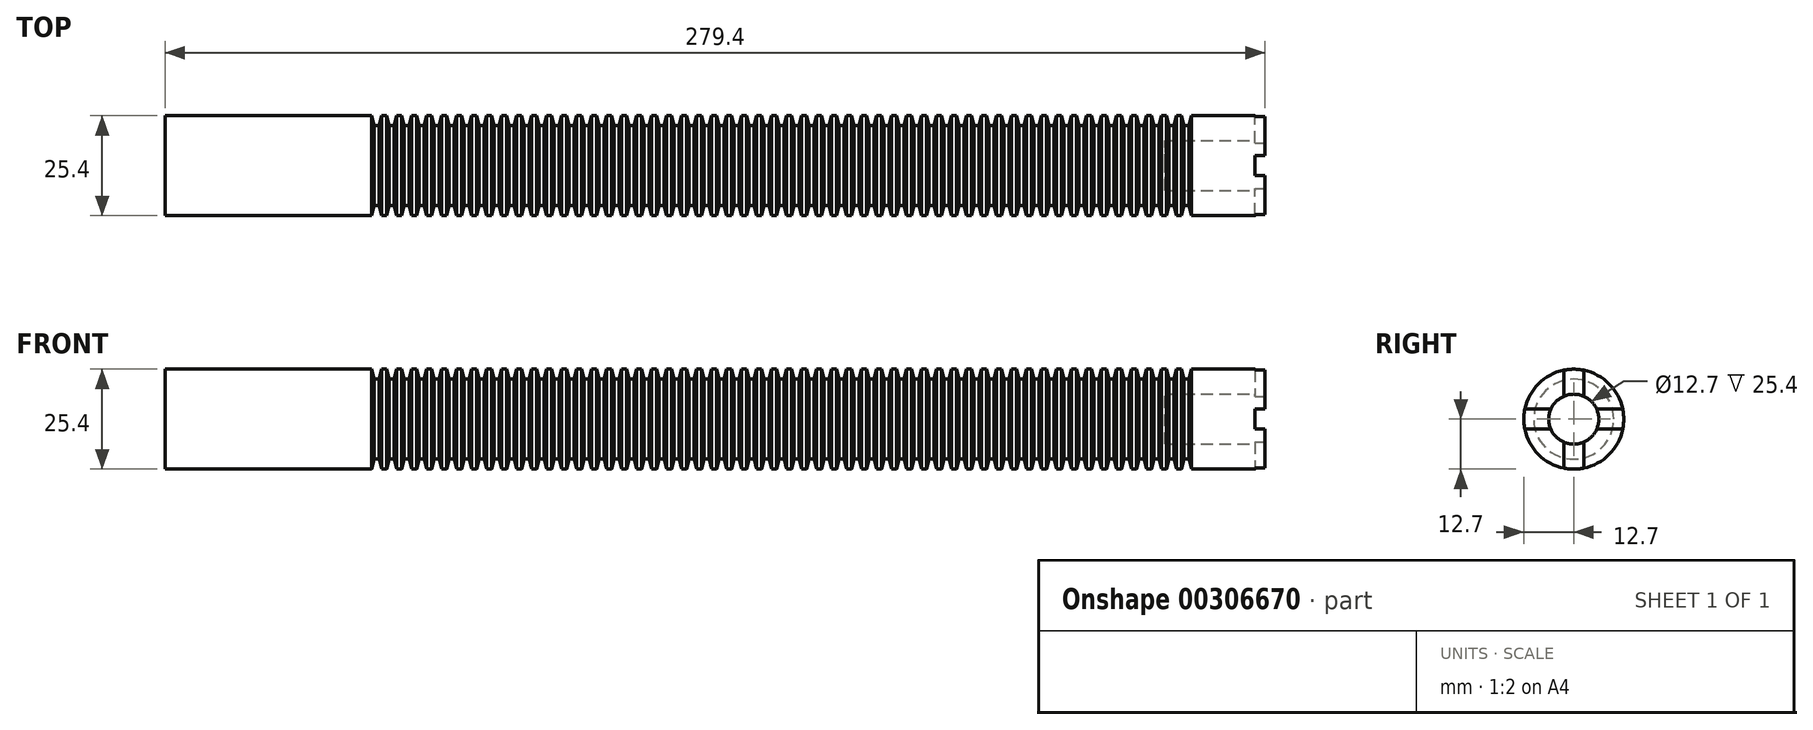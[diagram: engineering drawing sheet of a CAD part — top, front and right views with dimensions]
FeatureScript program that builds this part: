
annotation { "Feature Type Name" : "Feature", "Feature Type Description" : "" }
export const myFeature = defineFeature(function(context is Context, id is Id, definition is map)
    precondition{}
    {
        {
            var Q0;
            Q0=qCreatedBy(makeId("Front.planeOp"),FACE);
            var sketch = newSketch(context, id + "F0", { "sketchPlane" : qUnion([Q0])});
            skLineSegment(sketch, "E0", {"start": v(0, 0) * mm, "end": v(0, 12.7) * mm});
            skLineSegment(sketch, "E1", {"start": v(0, 12.7) * mm, "end": v(279.4, 12.7) * mm});
            skLineSegment(sketch, "E2", {"start": v(279.4, 12.7) * mm, "end": v(279.4, 0) * mm});
            skLineSegment(sketch, "E3", {"start": v(279.4, 0) * mm, "end": v(0, 0) * mm});
            skSolve(sketch);
        }
        {
            var Q0;
            Q0=makeQuery(id+"F0.imprint","IMPRINT",FACE,{"disambiguationData":[TD([[makeQuery(id+"F0.imprint","IMPRINT",EDGE,{"derivedFrom":sQuery(id+"F0.wireOp",EDGE,"E0")}),-1.0]])]});
            var Q1;
            Q1=sQuery(id+"F0.wireOp",EDGE,"E3");
            revolve(context, id + "F1", {"entities" : qUnion([Q0]), "axis" : qUnion([Q1]), "revolveType" : RevolveType.FULL});
        }
        {
            var Q0;
            Q0=makeQuery(id+"F1.opRevolve","SWEPT_FACE",FACE,{"disambiguationData":[OSD([sQuery(id+"F0.wireOp",EDGE,"E2")])]});
            var sketch = newSketch(context, id + "F2", { "sketchPlane" : qUnion([Q0])});
            skLineSegment(sketch, "E4.0", {"start": v(-12.7, -2.54) * mm, "end": v(-2.54, -2.54) * mm});
            skLineSegment(sketch, "E5.0", {"start": v(-12.7, 2.54) * mm, "end": v(-2.54, 2.54) * mm});
            skLineSegment(sketch, "E6.0", {"start": v(-2.54, 12.7) * mm, "end": v(-2.54, 2.54) * mm});
            skLineSegment(sketch, "E7.0", {"start": v(2.54, 12.7) * mm, "end": v(2.54, 2.54) * mm});
            skLineSegment(sketch, "E8.trimOffspring", {"start": v(2.54, 2.54) * mm, "end": v(12.7, 2.54) * mm});
            skLineSegment(sketch, "E9.trimOffspring", {"start": v(-2.54, -2.54) * mm, "end": v(-2.54, -12.7) * mm});
            skLineSegment(sketch, "E10.trimOffspring", {"start": v(2.54, -2.54) * mm, "end": v(12.7, -2.54) * mm});
            skLineSegment(sketch, "E11.trimOffspring", {"start": v(2.54, -2.54) * mm, "end": v(2.54, -12.7) * mm});
            skLineSegment(sketch, "E12", {"start": v(12.7, 2.54) * mm, "end": v(12.7, -2.54) * mm});
            skLineSegment(sketch, "E13", {"start": v(2.54, -12.7) * mm, "end": v(-2.54, -12.7) * mm});
            skLineSegment(sketch, "E14", {"start": v(-12.7, -2.54) * mm, "end": v(-12.7, 2.54) * mm});
            skLineSegment(sketch, "E15", {"start": v(-2.54, 12.7) * mm, "end": v(2.54, 12.7) * mm});
            skSolve(sketch);
        }
        {
            var Q0;
            {var subQ0=sQuery(id+"F2.wireOp",EDGE,"E14");var subQ1=sQuery(id+"F2.wireOp",EDGE,"E4.0");var subQ2=makeQuery(id+"F2.imprint","INTERSECT",VERTEX,{"derivedFrom":[subQ1,subQ0]});Q0=makeQuery(id+"F2.imprint","IMPRINT",FACE,{"disambiguationData":[TD([[makeQuery(id+"F2.imprint","IMPRINT",EDGE,{"disambiguationData":[TD([[subQ2,-1.0]])],"derivedFrom":subQ1}),1.0]])]});}
            var Q1;
            {var subQ0=sQuery(id+"F2.wireOp",EDGE,"E14");var subQ1=sQuery(id+"F2.wireOp",EDGE,"E5.0");var subQ2=makeQuery(id+"F2.imprint","INTERSECT",VERTEX,{"derivedFrom":[subQ1,subQ0]});Q1=makeQuery(id+"F2.imprint","IMPRINT",FACE,{"disambiguationData":[TD([[makeQuery(id+"F2.imprint","IMPRINT",EDGE,{"disambiguationData":[TD([[subQ2,-1.0]])],"derivedFrom":subQ1}),-1.0]])]});}
            var Q2;
            {var subQ0=sQuery(id+"F2.wireOp",EDGE,"E15");var subQ1=sQuery(id+"F2.wireOp",EDGE,"E6.0");var subQ2=makeQuery(id+"F2.imprint","INTERSECT",VERTEX,{"derivedFrom":[subQ1,subQ0]});Q2=makeQuery(id+"F2.imprint","IMPRINT",FACE,{"disambiguationData":[TD([[makeQuery(id+"F2.imprint","IMPRINT",EDGE,{"disambiguationData":[TD([[subQ2,-1.0]])],"derivedFrom":subQ1}),1.0]])]});}
            var Q3;
            {var subQ0=sQuery(id+"F2.wireOp",EDGE,"E15");var subQ1=sQuery(id+"F2.wireOp",EDGE,"E7.0");var subQ2=makeQuery(id+"F2.imprint","INTERSECT",VERTEX,{"derivedFrom":[subQ1,subQ0]});Q3=makeQuery(id+"F2.imprint","IMPRINT",FACE,{"disambiguationData":[TD([[makeQuery(id+"F2.imprint","IMPRINT",EDGE,{"disambiguationData":[TD([[subQ2,-1.0]])],"derivedFrom":subQ1}),-1.0]])]});}
            var Q4;
            {var subQ0=sQuery(id+"F2.wireOp",EDGE,"E12");var subQ1=sQuery(id+"F2.wireOp",EDGE,"E8.trimOffspring");var subQ2=makeQuery(id+"F2.imprint","INTERSECT",VERTEX,{"derivedFrom":[subQ1,subQ0]});Q4=makeQuery(id+"F2.imprint","IMPRINT",FACE,{"disambiguationData":[TD([[makeQuery(id+"F2.imprint","IMPRINT",EDGE,{"disambiguationData":[TD([[subQ2,1.0]])],"derivedFrom":subQ1}),-1.0]])]});}
            var Q5;
            {var subQ0=sQuery(id+"F2.wireOp",EDGE,"E13");var subQ1=sQuery(id+"F2.wireOp",EDGE,"E9.trimOffspring");var subQ2=makeQuery(id+"F2.imprint","INTERSECT",VERTEX,{"derivedFrom":[subQ1,subQ0]});Q5=makeQuery(id+"F2.imprint","IMPRINT",FACE,{"disambiguationData":[TD([[makeQuery(id+"F2.imprint","IMPRINT",EDGE,{"disambiguationData":[TD([[subQ2,1.0]])],"derivedFrom":subQ1}),1.0]])]});}
            var Q6;
            {var subQ0=sQuery(id+"F2.wireOp",EDGE,"E12");var subQ1=sQuery(id+"F2.wireOp",EDGE,"E10.trimOffspring");var subQ2=makeQuery(id+"F2.imprint","INTERSECT",VERTEX,{"derivedFrom":[subQ1,subQ0]});Q6=makeQuery(id+"F2.imprint","IMPRINT",FACE,{"disambiguationData":[TD([[makeQuery(id+"F2.imprint","IMPRINT",EDGE,{"disambiguationData":[TD([[subQ2,1.0]])],"derivedFrom":subQ1}),1.0]])]});}
            var Q7;
            {var subQ0=sQuery(id+"F2.wireOp",EDGE,"E13");var subQ1=sQuery(id+"F2.wireOp",EDGE,"E11.trimOffspring");var subQ2=makeQuery(id+"F2.imprint","INTERSECT",VERTEX,{"derivedFrom":[subQ1,subQ0]});Q7=makeQuery(id+"F2.imprint","IMPRINT",FACE,{"disambiguationData":[TD([[makeQuery(id+"F2.imprint","IMPRINT",EDGE,{"disambiguationData":[TD([[subQ2,1.0]])],"derivedFrom":subQ1}),-1.0]])]});}
            var Q8;
            {var subQ0=sQuery(id+"F2.wireOp",EDGE,"E4.0");var subQ8=sQuery(id+"F2.wireOp",EDGE,"E9.trimOffspring");var subQ9=makeQuery(id+"F2.imprint","INTERSECT",VERTEX,{"derivedFrom":[subQ0,subQ8]});Q8=makeQuery(id+"F2.imprint","IMPRINT",FACE,{"disambiguationData":[TD([[makeQuery(id+"F2.imprint","IMPRINT",EDGE,{"disambiguationData":[TD([[subQ9,1.0]])],"derivedFrom":subQ0}),1.0]])]});}
            extrude(context, id + "F3", {"entities" : qUnion([Q0, Q1, Q2, Q3, Q4, Q5, Q6, Q7, Q8]), "operationType" : NewBodyOperationType.REMOVE, "oppositeDirection" : true, "depth" : 2.54 * mm});
        }
        {
            var Q0;
            Q0=makeQuery(id+"F3.boolean.opBoolean","SPLIT",FACE,{"disambiguationData":[TD([makeQuery(id+"F3.opExtrude","SWEPT_FACE",FACE,{"disambiguationData":[OSD([sQuery(id+"F2.wireOp",EDGE,"E5.0")])]})])],"derivedFrom":makeQuery(id+"F1.opRevolve","SWEPT_FACE",FACE,{"disambiguationData":[OSD([sQuery(id+"F0.wireOp",EDGE,"E2")])]})});
            var sketch = newSketch(context, id + "F4", { "sketchPlane" : qUnion([Q0])});
            skArc(sketch, "E16.0", {"start": v(-2.54, 12.44) * mm, "mid": v(-8.98, 8.98) * mm, "end": v(-12.44, 2.54) * mm});
            skCircle(sketch, "E17", {"center": v(0, 0) * mm, "radius": 6.35 * mm});
            skSolve(sketch);
        }
        {
            var Q0;
            {var subQ0=sQuery(id+"F4.wireOp",EDGE,"E17");var subQ1=makeQuery(id+"F3.boolean.opBoolean","COPY",EDGE,{"derivedFrom":makeQuery(id+"F3.opExtrude","CAP_EDGE",EDGE,{"disambiguationData":[OSD([sQuery(id+"F2.wireOp",EDGE,"E5.0")])],"isStart":true})});var subQ2=makeQuery(id+"F4.imprint","INTERSECT",VERTEX,{"derivedFrom":[subQ1,subQ0]});Q0=makeQuery(id+"F4.imprint","IMPRINT",FACE,{"disambiguationData":[TD([[makeQuery(id+"F4.imprint","IMPRINT",EDGE,{"disambiguationData":[TD([[subQ2,1.0]])],"derivedFrom":subQ0}),1.0]])]});}
            var Q1;
            {var subQ0=sQuery(id+"F4.wireOp",EDGE,"E17");var subQ1=makeQuery(id+"F3.boolean.opBoolean","COPY",EDGE,{"derivedFrom":makeQuery(id+"F3.opExtrude","CAP_EDGE",EDGE,{"disambiguationData":[OSD([sQuery(id+"F2.wireOp",EDGE,"E5.0")])],"isStart":true})});var subQ2=makeQuery(id+"F4.imprint","INTERSECT",VERTEX,{"derivedFrom":[subQ1,subQ0]});Q1=makeQuery(id+"F4.imprint","IMPRINT",FACE,{"disambiguationData":[TD([[makeQuery(id+"F4.imprint","IMPRINT",EDGE,{"disambiguationData":[TD([[subQ2,-1.0]])],"derivedFrom":subQ0}),1.0]])]});}
            extrude(context, id + "F5", {"entities" : qUnion([Q0, Q1]), "operationType" : NewBodyOperationType.REMOVE, "oppositeDirection" : true, "depth" : 25.4 * mm});
        }
        {
            var Q0;
            Q0=qCreatedBy(makeId("Front.planeOp"),FACE);
            var sketch = newSketch(context, id + "F6", { "sketchPlane" : qUnion([Q0])});
            skLineSegment(sketch, "E18", {"start": v(276.86, -12.7) * mm, "end": v(0, -12.7) * mm});
            skLineSegment(sketch, "E19", {"start": v(279.4, 12.7) * mm, "end": v(260.35, 12.7) * mm, "construction": true});
            skLineSegment(sketch, "E20", {"start": v(260.35, 12.7) * mm, "end": v(260.35, -12.7) * mm, "construction": true});
            skLineSegment(sketch, "E21", {"start": v(0.03, 12.7) * mm, "end": v(52.48, 12.7) * mm, "construction": true});
            skLineSegment(sketch, "E22", {"start": v(52.48, 12.7) * mm, "end": v(52.48, 10.16) * mm, "construction": true});
            skLineSegment(sketch, "E23", {"start": v(52.48, 12.7) * mm, "end": v(53.12, 10.16) * mm});
            skLineSegment(sketch, "E24", {"start": v(53.12, 10.16) * mm, "end": v(54.39, 10.16) * mm});
            skLineSegment(sketch, "E25", {"start": v(54.39, 10.16) * mm, "end": v(55.02, 12.7) * mm});
            skLineSegment(sketch, "E26", {"start": v(55.02, 12.7) * mm, "end": v(52.48, 12.7) * mm});
            skLineSegment(sketch, "E27", {"start": v(52.48, 12.7) * mm, "end": v(55.02, 12.7) * mm});
            skLineSegment(sketch, "E28.1.0.0", {"start": v(58.2, 10.16) * mm, "end": v(58.83, 12.7) * mm});
            skLineSegment(sketch, "E28.1.0.1", {"start": v(56.93, 10.16) * mm, "end": v(58.2, 10.16) * mm});
            skLineSegment(sketch, "E28.1.0.2", {"start": v(56.3, 12.7) * mm, "end": v(56.93, 10.16) * mm});
            skLineSegment(sketch, "E28.1.0.3", {"start": v(56.3, 12.7) * mm, "end": v(58.83, 12.7) * mm});
            skLineSegment(sketch, "E28.2.0.0", {"start": v(62, 10.16) * mm, "end": v(62.64, 12.7) * mm});
            skLineSegment(sketch, "E28.2.0.1", {"start": v(60.74, 10.16) * mm, "end": v(62, 10.16) * mm});
            skLineSegment(sketch, "E28.2.0.2", {"start": v(60.1, 12.7) * mm, "end": v(60.74, 10.16) * mm});
            skLineSegment(sketch, "E28.2.0.3", {"start": v(60.1, 12.7) * mm, "end": v(62.64, 12.7) * mm});
            skLineSegment(sketch, "E28.3.0.0", {"start": v(65.82, 10.16) * mm, "end": v(66.45, 12.7) * mm});
            skLineSegment(sketch, "E28.3.0.1", {"start": v(64.55, 10.16) * mm, "end": v(65.82, 10.16) * mm});
            skLineSegment(sketch, "E28.3.0.2", {"start": v(63.91, 12.7) * mm, "end": v(64.55, 10.16) * mm});
            skLineSegment(sketch, "E28.3.0.3", {"start": v(63.91, 12.7) * mm, "end": v(66.45, 12.7) * mm});
            skLineSegment(sketch, "E28.4.0.0", {"start": v(69.63, 10.16) * mm, "end": v(70.26, 12.7) * mm});
            skLineSegment(sketch, "E28.4.0.1", {"start": v(68.36, 10.16) * mm, "end": v(69.63, 10.16) * mm});
            skLineSegment(sketch, "E28.4.0.2", {"start": v(67.72, 12.7) * mm, "end": v(68.36, 10.16) * mm});
            skLineSegment(sketch, "E28.4.0.3", {"start": v(67.72, 12.7) * mm, "end": v(70.26, 12.7) * mm});
            skLineSegment(sketch, "E28.5.0.0", {"start": v(73.44, 10.16) * mm, "end": v(74.07, 12.7) * mm});
            skLineSegment(sketch, "E28.5.0.1", {"start": v(72.17, 10.16) * mm, "end": v(73.44, 10.16) * mm});
            skLineSegment(sketch, "E28.5.0.2", {"start": v(71.53, 12.7) * mm, "end": v(72.17, 10.16) * mm});
            skLineSegment(sketch, "E28.5.0.3", {"start": v(71.53, 12.7) * mm, "end": v(74.07, 12.7) * mm});
            skLineSegment(sketch, "E28.6.0.0", {"start": v(77.25, 10.16) * mm, "end": v(77.88, 12.7) * mm});
            skLineSegment(sketch, "E28.6.0.1", {"start": v(75.98, 10.16) * mm, "end": v(77.25, 10.16) * mm});
            skLineSegment(sketch, "E28.6.0.2", {"start": v(75.34, 12.7) * mm, "end": v(75.98, 10.16) * mm});
            skLineSegment(sketch, "E28.6.0.3", {"start": v(75.34, 12.7) * mm, "end": v(77.88, 12.7) * mm});
            skLineSegment(sketch, "E28.7.0.0", {"start": v(81.06, 10.16) * mm, "end": v(81.7, 12.7) * mm});
            skLineSegment(sketch, "E28.7.0.1", {"start": v(79.8, 10.16) * mm, "end": v(81.06, 10.16) * mm});
            skLineSegment(sketch, "E28.7.0.2", {"start": v(79.15, 12.7) * mm, "end": v(79.8, 10.16) * mm});
            skLineSegment(sketch, "E28.7.0.3", {"start": v(79.15, 12.7) * mm, "end": v(81.7, 12.7) * mm});
            skLineSegment(sketch, "E28.8.0.0", {"start": v(84.87, 10.16) * mm, "end": v(85.5, 12.7) * mm});
            skLineSegment(sketch, "E28.8.0.1", {"start": v(83.6, 10.16) * mm, "end": v(84.87, 10.16) * mm});
            skLineSegment(sketch, "E28.8.0.2", {"start": v(82.96, 12.7) * mm, "end": v(83.6, 10.16) * mm});
            skLineSegment(sketch, "E28.8.0.3", {"start": v(82.96, 12.7) * mm, "end": v(85.5, 12.7) * mm});
            skLineSegment(sketch, "E28.9.0.0", {"start": v(88.68, 10.16) * mm, "end": v(89.31, 12.7) * mm});
            skLineSegment(sketch, "E28.9.0.1", {"start": v(87.41, 10.16) * mm, "end": v(88.68, 10.16) * mm});
            skLineSegment(sketch, "E28.9.0.2", {"start": v(86.77, 12.7) * mm, "end": v(87.41, 10.16) * mm});
            skLineSegment(sketch, "E28.9.0.3", {"start": v(86.77, 12.7) * mm, "end": v(89.31, 12.7) * mm});
            skLineSegment(sketch, "E28.10.0.0", {"start": v(92.49, 10.16) * mm, "end": v(93.12, 12.7) * mm});
            skLineSegment(sketch, "E28.10.0.1", {"start": v(91.22, 10.16) * mm, "end": v(92.49, 10.16) * mm});
            skLineSegment(sketch, "E28.10.0.2", {"start": v(90.58, 12.7) * mm, "end": v(91.22, 10.16) * mm});
            skLineSegment(sketch, "E28.10.0.3", {"start": v(90.58, 12.7) * mm, "end": v(93.12, 12.7) * mm});
            skLineSegment(sketch, "E28.11.0.0", {"start": v(96.3, 10.16) * mm, "end": v(96.93, 12.7) * mm});
            skLineSegment(sketch, "E28.11.0.1", {"start": v(95.03, 10.16) * mm, "end": v(96.3, 10.16) * mm});
            skLineSegment(sketch, "E28.11.0.2", {"start": v(94.4, 12.7) * mm, "end": v(95.03, 10.16) * mm});
            skLineSegment(sketch, "E28.11.0.3", {"start": v(94.4, 12.7) * mm, "end": v(96.93, 12.7) * mm});
            skLineSegment(sketch, "E28.12.0.0", {"start": v(100.1, 10.16) * mm, "end": v(100.74, 12.7) * mm});
            skLineSegment(sketch, "E28.12.0.1", {"start": v(98.84, 10.16) * mm, "end": v(100.1, 10.16) * mm});
            skLineSegment(sketch, "E28.12.0.2", {"start": v(98.2, 12.7) * mm, "end": v(98.84, 10.16) * mm});
            skLineSegment(sketch, "E28.12.0.3", {"start": v(98.2, 12.7) * mm, "end": v(100.74, 12.7) * mm});
            skLineSegment(sketch, "E28.13.0.0", {"start": v(103.92, 10.16) * mm, "end": v(104.55, 12.7) * mm});
            skLineSegment(sketch, "E28.13.0.1", {"start": v(102.65, 10.16) * mm, "end": v(103.92, 10.16) * mm});
            skLineSegment(sketch, "E28.13.0.2", {"start": v(102.01, 12.7) * mm, "end": v(102.65, 10.16) * mm});
            skLineSegment(sketch, "E28.13.0.3", {"start": v(102.01, 12.7) * mm, "end": v(104.55, 12.7) * mm});
            skLineSegment(sketch, "E28.14.0.0", {"start": v(107.73, 10.16) * mm, "end": v(108.36, 12.7) * mm});
            skLineSegment(sketch, "E28.14.0.1", {"start": v(106.46, 10.16) * mm, "end": v(107.73, 10.16) * mm});
            skLineSegment(sketch, "E28.14.0.2", {"start": v(105.82, 12.7) * mm, "end": v(106.46, 10.16) * mm});
            skLineSegment(sketch, "E28.14.0.3", {"start": v(105.82, 12.7) * mm, "end": v(108.36, 12.7) * mm});
            skLineSegment(sketch, "E28.15.0.0", {"start": v(111.54, 10.16) * mm, "end": v(112.17, 12.7) * mm});
            skLineSegment(sketch, "E28.15.0.1", {"start": v(110.27, 10.16) * mm, "end": v(111.54, 10.16) * mm});
            skLineSegment(sketch, "E28.15.0.2", {"start": v(109.63, 12.7) * mm, "end": v(110.27, 10.16) * mm});
            skLineSegment(sketch, "E28.15.0.3", {"start": v(109.63, 12.7) * mm, "end": v(112.17, 12.7) * mm});
            skLineSegment(sketch, "E28.16.0.0", {"start": v(115.35, 10.16) * mm, "end": v(115.98, 12.7) * mm});
            skLineSegment(sketch, "E28.16.0.1", {"start": v(114.08, 10.16) * mm, "end": v(115.35, 10.16) * mm});
            skLineSegment(sketch, "E28.16.0.2", {"start": v(113.44, 12.7) * mm, "end": v(114.08, 10.16) * mm});
            skLineSegment(sketch, "E28.16.0.3", {"start": v(113.44, 12.7) * mm, "end": v(115.98, 12.7) * mm});
            skLineSegment(sketch, "E28.17.0.0", {"start": v(119.16, 10.16) * mm, "end": v(119.8, 12.7) * mm});
            skLineSegment(sketch, "E28.17.0.1", {"start": v(117.9, 10.16) * mm, "end": v(119.16, 10.16) * mm});
            skLineSegment(sketch, "E28.17.0.2", {"start": v(117.25, 12.7) * mm, "end": v(117.9, 10.16) * mm});
            skLineSegment(sketch, "E28.17.0.3", {"start": v(117.25, 12.7) * mm, "end": v(119.8, 12.7) * mm});
            skLineSegment(sketch, "E28.18.0.0", {"start": v(122.97, 10.16) * mm, "end": v(123.6, 12.7) * mm});
            skLineSegment(sketch, "E28.18.0.1", {"start": v(121.7, 10.16) * mm, "end": v(122.97, 10.16) * mm});
            skLineSegment(sketch, "E28.18.0.2", {"start": v(121.06, 12.7) * mm, "end": v(121.7, 10.16) * mm});
            skLineSegment(sketch, "E28.18.0.3", {"start": v(121.06, 12.7) * mm, "end": v(123.6, 12.7) * mm});
            skLineSegment(sketch, "E28.19.0.0", {"start": v(126.78, 10.16) * mm, "end": v(127.41, 12.7) * mm});
            skLineSegment(sketch, "E28.19.0.1", {"start": v(125.51, 10.16) * mm, "end": v(126.78, 10.16) * mm});
            skLineSegment(sketch, "E28.19.0.2", {"start": v(124.87, 12.7) * mm, "end": v(125.51, 10.16) * mm});
            skLineSegment(sketch, "E28.19.0.3", {"start": v(124.87, 12.7) * mm, "end": v(127.41, 12.7) * mm});
            skLineSegment(sketch, "E28.20.0.0", {"start": v(130.59, 10.16) * mm, "end": v(131.22, 12.7) * mm});
            skLineSegment(sketch, "E28.20.0.1", {"start": v(129.32, 10.16) * mm, "end": v(130.59, 10.16) * mm});
            skLineSegment(sketch, "E28.20.0.2", {"start": v(128.68, 12.7) * mm, "end": v(129.32, 10.16) * mm});
            skLineSegment(sketch, "E28.20.0.3", {"start": v(128.68, 12.7) * mm, "end": v(131.22, 12.7) * mm});
            skLineSegment(sketch, "E28.21.0.0", {"start": v(134.4, 10.16) * mm, "end": v(135.03, 12.7) * mm});
            skLineSegment(sketch, "E28.21.0.1", {"start": v(133.13, 10.16) * mm, "end": v(134.4, 10.16) * mm});
            skLineSegment(sketch, "E28.21.0.2", {"start": v(132.5, 12.7) * mm, "end": v(133.13, 10.16) * mm});
            skLineSegment(sketch, "E28.21.0.3", {"start": v(132.5, 12.7) * mm, "end": v(135.03, 12.7) * mm});
            skLineSegment(sketch, "E28.22.0.0", {"start": v(138.2, 10.16) * mm, "end": v(138.84, 12.7) * mm});
            skLineSegment(sketch, "E28.22.0.1", {"start": v(136.94, 10.16) * mm, "end": v(138.2, 10.16) * mm});
            skLineSegment(sketch, "E28.22.0.2", {"start": v(136.3, 12.7) * mm, "end": v(136.94, 10.16) * mm});
            skLineSegment(sketch, "E28.22.0.3", {"start": v(136.3, 12.7) * mm, "end": v(138.84, 12.7) * mm});
            skLineSegment(sketch, "E28.23.0.0", {"start": v(142.02, 10.16) * mm, "end": v(142.65, 12.7) * mm});
            skLineSegment(sketch, "E28.23.0.1", {"start": v(140.75, 10.16) * mm, "end": v(142.02, 10.16) * mm});
            skLineSegment(sketch, "E28.23.0.2", {"start": v(140.11, 12.7) * mm, "end": v(140.75, 10.16) * mm});
            skLineSegment(sketch, "E28.23.0.3", {"start": v(140.11, 12.7) * mm, "end": v(142.65, 12.7) * mm});
            skLineSegment(sketch, "E28.24.0.0", {"start": v(145.83, 10.16) * mm, "end": v(146.46, 12.7) * mm});
            skLineSegment(sketch, "E28.24.0.1", {"start": v(144.56, 10.16) * mm, "end": v(145.83, 10.16) * mm});
            skLineSegment(sketch, "E28.24.0.2", {"start": v(143.92, 12.7) * mm, "end": v(144.56, 10.16) * mm});
            skLineSegment(sketch, "E28.24.0.3", {"start": v(143.92, 12.7) * mm, "end": v(146.46, 12.7) * mm});
            skLineSegment(sketch, "E28.25.0.0", {"start": v(149.64, 10.16) * mm, "end": v(150.27, 12.7) * mm});
            skLineSegment(sketch, "E28.25.0.1", {"start": v(148.37, 10.16) * mm, "end": v(149.64, 10.16) * mm});
            skLineSegment(sketch, "E28.25.0.2", {"start": v(147.73, 12.7) * mm, "end": v(148.37, 10.16) * mm});
            skLineSegment(sketch, "E28.25.0.3", {"start": v(147.73, 12.7) * mm, "end": v(150.27, 12.7) * mm});
            skLineSegment(sketch, "E28.26.0.0", {"start": v(153.45, 10.16) * mm, "end": v(154.08, 12.7) * mm});
            skLineSegment(sketch, "E28.26.0.1", {"start": v(152.18, 10.16) * mm, "end": v(153.45, 10.16) * mm});
            skLineSegment(sketch, "E28.26.0.2", {"start": v(151.54, 12.7) * mm, "end": v(152.18, 10.16) * mm});
            skLineSegment(sketch, "E28.26.0.3", {"start": v(151.54, 12.7) * mm, "end": v(154.08, 12.7) * mm});
            skLineSegment(sketch, "E28.27.0.0", {"start": v(157.26, 10.16) * mm, "end": v(157.9, 12.7) * mm});
            skLineSegment(sketch, "E28.27.0.1", {"start": v(156, 10.16) * mm, "end": v(157.26, 10.16) * mm});
            skLineSegment(sketch, "E28.27.0.2", {"start": v(155.35, 12.7) * mm, "end": v(156, 10.16) * mm});
            skLineSegment(sketch, "E28.27.0.3", {"start": v(155.35, 12.7) * mm, "end": v(157.9, 12.7) * mm});
            skLineSegment(sketch, "E28.28.0.0", {"start": v(161.07, 10.16) * mm, "end": v(161.7, 12.7) * mm});
            skLineSegment(sketch, "E28.28.0.1", {"start": v(159.8, 10.16) * mm, "end": v(161.07, 10.16) * mm});
            skLineSegment(sketch, "E28.28.0.2", {"start": v(159.16, 12.7) * mm, "end": v(159.8, 10.16) * mm});
            skLineSegment(sketch, "E28.28.0.3", {"start": v(159.16, 12.7) * mm, "end": v(161.7, 12.7) * mm});
            skLineSegment(sketch, "E28.29.0.0", {"start": v(164.88, 10.16) * mm, "end": v(165.51, 12.7) * mm});
            skLineSegment(sketch, "E28.29.0.1", {"start": v(163.61, 10.16) * mm, "end": v(164.88, 10.16) * mm});
            skLineSegment(sketch, "E28.29.0.2", {"start": v(162.97, 12.7) * mm, "end": v(163.61, 10.16) * mm});
            skLineSegment(sketch, "E28.29.0.3", {"start": v(162.97, 12.7) * mm, "end": v(165.51, 12.7) * mm});
            skLineSegment(sketch, "E28.30.0.0", {"start": v(168.69, 10.16) * mm, "end": v(169.32, 12.7) * mm});
            skLineSegment(sketch, "E28.30.0.1", {"start": v(167.42, 10.16) * mm, "end": v(168.69, 10.16) * mm});
            skLineSegment(sketch, "E28.30.0.2", {"start": v(166.78, 12.7) * mm, "end": v(167.42, 10.16) * mm});
            skLineSegment(sketch, "E28.30.0.3", {"start": v(166.78, 12.7) * mm, "end": v(169.32, 12.7) * mm});
            skLineSegment(sketch, "E28.31.0.0", {"start": v(172.5, 10.16) * mm, "end": v(173.13, 12.7) * mm});
            skLineSegment(sketch, "E28.31.0.1", {"start": v(171.23, 10.16) * mm, "end": v(172.5, 10.16) * mm});
            skLineSegment(sketch, "E28.31.0.2", {"start": v(170.6, 12.7) * mm, "end": v(171.23, 10.16) * mm});
            skLineSegment(sketch, "E28.31.0.3", {"start": v(170.6, 12.7) * mm, "end": v(173.13, 12.7) * mm});
            skLineSegment(sketch, "E28.32.0.0", {"start": v(176.3, 10.16) * mm, "end": v(176.94, 12.7) * mm});
            skLineSegment(sketch, "E28.32.0.1", {"start": v(175.04, 10.16) * mm, "end": v(176.3, 10.16) * mm});
            skLineSegment(sketch, "E28.32.0.2", {"start": v(174.4, 12.7) * mm, "end": v(175.04, 10.16) * mm});
            skLineSegment(sketch, "E28.32.0.3", {"start": v(174.4, 12.7) * mm, "end": v(176.94, 12.7) * mm});
            skLineSegment(sketch, "E28.33.0.0", {"start": v(180.12, 10.16) * mm, "end": v(180.75, 12.7) * mm});
            skLineSegment(sketch, "E28.33.0.1", {"start": v(178.85, 10.16) * mm, "end": v(180.12, 10.16) * mm});
            skLineSegment(sketch, "E28.33.0.2", {"start": v(178.21, 12.7) * mm, "end": v(178.85, 10.16) * mm});
            skLineSegment(sketch, "E28.33.0.3", {"start": v(178.21, 12.7) * mm, "end": v(180.75, 12.7) * mm});
            skLineSegment(sketch, "E28.34.0.0", {"start": v(183.93, 10.16) * mm, "end": v(184.56, 12.7) * mm});
            skLineSegment(sketch, "E28.34.0.1", {"start": v(182.66, 10.16) * mm, "end": v(183.93, 10.16) * mm});
            skLineSegment(sketch, "E28.34.0.2", {"start": v(182.02, 12.7) * mm, "end": v(182.66, 10.16) * mm});
            skLineSegment(sketch, "E28.34.0.3", {"start": v(182.02, 12.7) * mm, "end": v(184.56, 12.7) * mm});
            skLineSegment(sketch, "E28.35.0.0", {"start": v(187.74, 10.16) * mm, "end": v(188.37, 12.7) * mm});
            skLineSegment(sketch, "E28.35.0.1", {"start": v(186.47, 10.16) * mm, "end": v(187.74, 10.16) * mm});
            skLineSegment(sketch, "E28.35.0.2", {"start": v(185.83, 12.7) * mm, "end": v(186.47, 10.16) * mm});
            skLineSegment(sketch, "E28.35.0.3", {"start": v(185.83, 12.7) * mm, "end": v(188.37, 12.7) * mm});
            skLineSegment(sketch, "E28.36.0.0", {"start": v(191.55, 10.16) * mm, "end": v(192.18, 12.7) * mm});
            skLineSegment(sketch, "E28.36.0.1", {"start": v(190.28, 10.16) * mm, "end": v(191.55, 10.16) * mm});
            skLineSegment(sketch, "E28.36.0.2", {"start": v(189.64, 12.7) * mm, "end": v(190.28, 10.16) * mm});
            skLineSegment(sketch, "E28.36.0.3", {"start": v(189.64, 12.7) * mm, "end": v(192.18, 12.7) * mm});
            skLineSegment(sketch, "E28.37.0.0", {"start": v(195.36, 10.16) * mm, "end": v(196, 12.7) * mm});
            skLineSegment(sketch, "E28.37.0.1", {"start": v(194.1, 10.16) * mm, "end": v(195.36, 10.16) * mm});
            skLineSegment(sketch, "E28.37.0.2", {"start": v(193.45, 12.7) * mm, "end": v(194.1, 10.16) * mm});
            skLineSegment(sketch, "E28.37.0.3", {"start": v(193.45, 12.7) * mm, "end": v(196, 12.7) * mm});
            skLineSegment(sketch, "E28.38.0.0", {"start": v(199.17, 10.16) * mm, "end": v(199.8, 12.7) * mm});
            skLineSegment(sketch, "E28.38.0.1", {"start": v(197.9, 10.16) * mm, "end": v(199.17, 10.16) * mm});
            skLineSegment(sketch, "E28.38.0.2", {"start": v(197.26, 12.7) * mm, "end": v(197.9, 10.16) * mm});
            skLineSegment(sketch, "E28.38.0.3", {"start": v(197.26, 12.7) * mm, "end": v(199.8, 12.7) * mm});
            skLineSegment(sketch, "E28.39.0.0", {"start": v(202.98, 10.16) * mm, "end": v(203.61, 12.7) * mm});
            skLineSegment(sketch, "E28.39.0.1", {"start": v(201.71, 10.16) * mm, "end": v(202.98, 10.16) * mm});
            skLineSegment(sketch, "E28.39.0.2", {"start": v(201.07, 12.7) * mm, "end": v(201.71, 10.16) * mm});
            skLineSegment(sketch, "E28.39.0.3", {"start": v(201.07, 12.7) * mm, "end": v(203.61, 12.7) * mm});
            skLineSegment(sketch, "E28.40.0.0", {"start": v(206.79, 10.16) * mm, "end": v(207.42, 12.7) * mm});
            skLineSegment(sketch, "E28.40.0.1", {"start": v(205.52, 10.16) * mm, "end": v(206.79, 10.16) * mm});
            skLineSegment(sketch, "E28.40.0.2", {"start": v(204.88, 12.7) * mm, "end": v(205.52, 10.16) * mm});
            skLineSegment(sketch, "E28.40.0.3", {"start": v(204.88, 12.7) * mm, "end": v(207.42, 12.7) * mm});
            skLineSegment(sketch, "E28.41.0.0", {"start": v(210.6, 10.16) * mm, "end": v(211.23, 12.7) * mm});
            skLineSegment(sketch, "E28.41.0.1", {"start": v(209.33, 10.16) * mm, "end": v(210.6, 10.16) * mm});
            skLineSegment(sketch, "E28.41.0.2", {"start": v(208.7, 12.7) * mm, "end": v(209.33, 10.16) * mm});
            skLineSegment(sketch, "E28.41.0.3", {"start": v(208.7, 12.7) * mm, "end": v(211.23, 12.7) * mm});
            skLineSegment(sketch, "E28.42.0.0", {"start": v(214.4, 10.16) * mm, "end": v(215.04, 12.7) * mm});
            skLineSegment(sketch, "E28.42.0.1", {"start": v(213.14, 10.16) * mm, "end": v(214.4, 10.16) * mm});
            skLineSegment(sketch, "E28.42.0.2", {"start": v(212.5, 12.7) * mm, "end": v(213.14, 10.16) * mm});
            skLineSegment(sketch, "E28.42.0.3", {"start": v(212.5, 12.7) * mm, "end": v(215.04, 12.7) * mm});
            skLineSegment(sketch, "E28.43.0.0", {"start": v(218.22, 10.16) * mm, "end": v(218.85, 12.7) * mm});
            skLineSegment(sketch, "E28.43.0.1", {"start": v(216.95, 10.16) * mm, "end": v(218.22, 10.16) * mm});
            skLineSegment(sketch, "E28.43.0.2", {"start": v(216.31, 12.7) * mm, "end": v(216.95, 10.16) * mm});
            skLineSegment(sketch, "E28.43.0.3", {"start": v(216.31, 12.7) * mm, "end": v(218.85, 12.7) * mm});
            skLineSegment(sketch, "E28.44.0.0", {"start": v(222.03, 10.16) * mm, "end": v(222.66, 12.7) * mm});
            skLineSegment(sketch, "E28.44.0.1", {"start": v(220.76, 10.16) * mm, "end": v(222.03, 10.16) * mm});
            skLineSegment(sketch, "E28.44.0.2", {"start": v(220.12, 12.7) * mm, "end": v(220.76, 10.16) * mm});
            skLineSegment(sketch, "E28.44.0.3", {"start": v(220.12, 12.7) * mm, "end": v(222.66, 12.7) * mm});
            skLineSegment(sketch, "E28.45.0.0", {"start": v(225.84, 10.16) * mm, "end": v(226.47, 12.7) * mm});
            skLineSegment(sketch, "E28.45.0.1", {"start": v(224.57, 10.16) * mm, "end": v(225.84, 10.16) * mm});
            skLineSegment(sketch, "E28.45.0.2", {"start": v(223.93, 12.7) * mm, "end": v(224.57, 10.16) * mm});
            skLineSegment(sketch, "E28.45.0.3", {"start": v(223.93, 12.7) * mm, "end": v(226.47, 12.7) * mm});
            skLineSegment(sketch, "E28.46.0.0", {"start": v(229.65, 10.16) * mm, "end": v(230.28, 12.7) * mm});
            skLineSegment(sketch, "E28.46.0.1", {"start": v(228.38, 10.16) * mm, "end": v(229.65, 10.16) * mm});
            skLineSegment(sketch, "E28.46.0.2", {"start": v(227.74, 12.7) * mm, "end": v(228.38, 10.16) * mm});
            skLineSegment(sketch, "E28.46.0.3", {"start": v(227.74, 12.7) * mm, "end": v(230.28, 12.7) * mm});
            skLineSegment(sketch, "E28.47.0.0", {"start": v(233.46, 10.16) * mm, "end": v(234.1, 12.7) * mm});
            skLineSegment(sketch, "E28.47.0.1", {"start": v(232.2, 10.16) * mm, "end": v(233.46, 10.16) * mm});
            skLineSegment(sketch, "E28.47.0.2", {"start": v(231.55, 12.7) * mm, "end": v(232.2, 10.16) * mm});
            skLineSegment(sketch, "E28.47.0.3", {"start": v(231.55, 12.7) * mm, "end": v(234.1, 12.7) * mm});
            skLineSegment(sketch, "E28.48.0.0", {"start": v(237.27, 10.16) * mm, "end": v(237.9, 12.7) * mm});
            skLineSegment(sketch, "E28.48.0.1", {"start": v(236, 10.16) * mm, "end": v(237.27, 10.16) * mm});
            skLineSegment(sketch, "E28.48.0.2", {"start": v(235.36, 12.7) * mm, "end": v(236, 10.16) * mm});
            skLineSegment(sketch, "E28.48.0.3", {"start": v(235.36, 12.7) * mm, "end": v(237.9, 12.7) * mm});
            skLineSegment(sketch, "E28.49.0.0", {"start": v(241.08, 10.16) * mm, "end": v(241.71, 12.7) * mm});
            skLineSegment(sketch, "E28.49.0.1", {"start": v(239.81, 10.16) * mm, "end": v(241.08, 10.16) * mm});
            skLineSegment(sketch, "E28.49.0.2", {"start": v(239.17, 12.7) * mm, "end": v(239.81, 10.16) * mm});
            skLineSegment(sketch, "E28.49.0.3", {"start": v(239.17, 12.7) * mm, "end": v(241.71, 12.7) * mm});
            skLineSegment(sketch, "E28.50.0.0", {"start": v(244.89, 10.16) * mm, "end": v(245.52, 12.7) * mm});
            skLineSegment(sketch, "E28.50.0.1", {"start": v(243.62, 10.16) * mm, "end": v(244.89, 10.16) * mm});
            skLineSegment(sketch, "E28.50.0.2", {"start": v(242.98, 12.7) * mm, "end": v(243.62, 10.16) * mm});
            skLineSegment(sketch, "E28.50.0.3", {"start": v(242.98, 12.7) * mm, "end": v(245.52, 12.7) * mm});
            skLineSegment(sketch, "E28.51.0.0", {"start": v(248.7, 10.16) * mm, "end": v(249.33, 12.7) * mm});
            skLineSegment(sketch, "E28.51.0.1", {"start": v(247.43, 10.16) * mm, "end": v(248.7, 10.16) * mm});
            skLineSegment(sketch, "E28.51.0.2", {"start": v(246.8, 12.7) * mm, "end": v(247.43, 10.16) * mm});
            skLineSegment(sketch, "E28.51.0.3", {"start": v(246.8, 12.7) * mm, "end": v(249.33, 12.7) * mm});
            skLineSegment(sketch, "E28.52.0.0", {"start": v(252.5, 10.16) * mm, "end": v(253.14, 12.7) * mm});
            skLineSegment(sketch, "E28.52.0.1", {"start": v(251.24, 10.16) * mm, "end": v(252.5, 10.16) * mm});
            skLineSegment(sketch, "E28.52.0.2", {"start": v(250.6, 12.7) * mm, "end": v(251.24, 10.16) * mm});
            skLineSegment(sketch, "E28.52.0.3", {"start": v(250.6, 12.7) * mm, "end": v(253.14, 12.7) * mm});
            skLineSegment(sketch, "E28.53.0.0", {"start": v(256.32, 10.16) * mm, "end": v(256.95, 12.7) * mm});
            skLineSegment(sketch, "E28.53.0.1", {"start": v(255.05, 10.16) * mm, "end": v(256.32, 10.16) * mm});
            skLineSegment(sketch, "E28.53.0.2", {"start": v(254.41, 12.7) * mm, "end": v(255.05, 10.16) * mm});
            skLineSegment(sketch, "E28.53.0.3", {"start": v(254.41, 12.7) * mm, "end": v(256.95, 12.7) * mm});
            skLineSegment(sketch, "E28.54.0.0", {"start": v(260.13, 10.16) * mm, "end": v(260.76, 12.7) * mm});
            skLineSegment(sketch, "E28.54.0.1", {"start": v(258.86, 10.16) * mm, "end": v(260.13, 10.16) * mm});
            skLineSegment(sketch, "E28.54.0.2", {"start": v(258.22, 12.7) * mm, "end": v(258.86, 10.16) * mm});
            skLineSegment(sketch, "E28.54.0.3", {"start": v(258.22, 12.7) * mm, "end": v(260.76, 12.7) * mm});
            skLineSegment(sketch, "E28.direction1", {"start": v(54.39, 10.16) * mm, "end": v(58.2, 10.16) * mm, "construction": true});
            skLineSegment(sketch, "E29", {"start": v(0, 0) * mm, "end": v(31.98, 0) * mm, "construction": true});
            skSolve(sketch);
        }
        {
            var Q0;
            Q0 = qSketchRegion(id + "F6", true);
            var Q1;
            Q1=sQuery(id+"F6.wireOp",EDGE,"E29");
            revolve(context, id + "F7", {"operationType" : NewBodyOperationType.REMOVE, "entities" : qUnion([Q0]), "axis" : qUnion([Q1]), "revolveType" : RevolveType.FULL, "oppositeDirection" : true});
        }
    });
